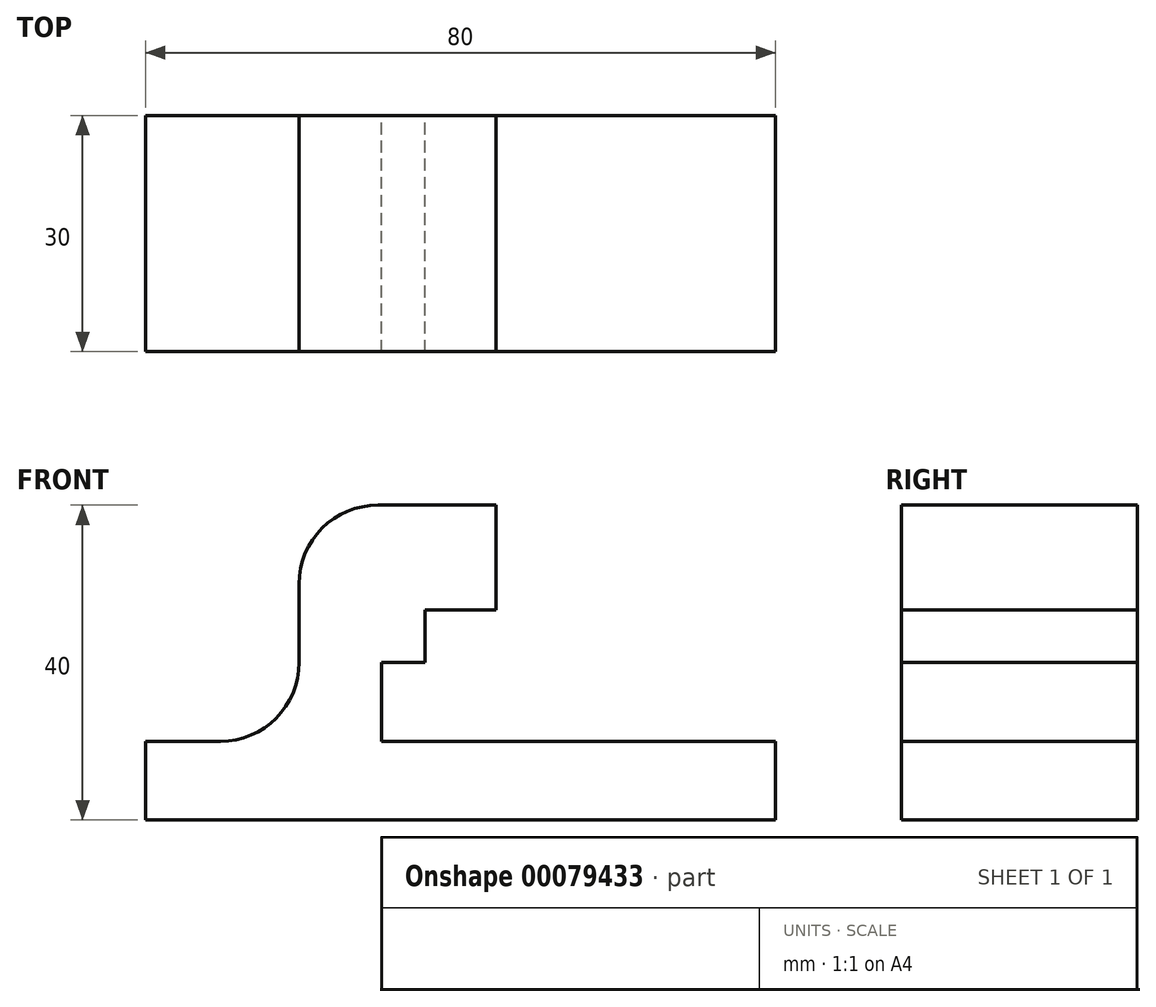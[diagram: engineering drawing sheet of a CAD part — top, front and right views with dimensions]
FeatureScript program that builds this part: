
annotation { "Feature Type Name" : "Feature", "Feature Type Description" : "" }
export const myFeature = defineFeature(function(context is Context, id is Id, definition is map)
    precondition{}
    {
        {
            var Q0;
            Q0=qCreatedBy(makeId("Front.planeOp"),FACE);
            var sketch = newSketch(context, id + "F0", { "sketchPlane" : qUnion([Q0])});
            skLineSegment(sketch, "E0", {"start": v(0, 0) * mm, "end": v(80, 0) * mm});
            skLineSegment(sketch, "E1", {"start": v(80, 0) * mm, "end": v(80, 10) * mm});
            skLineSegment(sketch, "E2", {"start": v(80, 10) * mm, "end": v(29.95, 10) * mm});
            skLineSegment(sketch, "E3", {"start": v(29.95, 10) * mm, "end": v(29.95, 20) * mm});
            skLineSegment(sketch, "E4", {"start": v(29.95, 20) * mm, "end": v(35.5, 20) * mm});
            skLineSegment(sketch, "E5", {"start": v(35.5, 20) * mm, "end": v(35.5, 26.7) * mm});
            skLineSegment(sketch, "E6", {"start": v(35.5, 26.7) * mm, "end": v(44.5, 26.7) * mm});
            skLineSegment(sketch, "E7", {"start": v(44.5, 26.7) * mm, "end": v(44.5, 40) * mm});
            skLineSegment(sketch, "E8", {"start": v(44.5, 40) * mm, "end": v(19.5, 40) * mm});
            skLineSegment(sketch, "E9", {"start": v(19.5, 40) * mm, "end": v(19.5, 10) * mm});
            skLineSegment(sketch, "E10", {"start": v(19.5, 10) * mm, "end": v(0, 10) * mm});
            skLineSegment(sketch, "E11", {"start": v(0, 10) * mm, "end": v(0, 0) * mm});
            skLineSegment(sketch, "E12", {"start": v(50.05, 10) * mm, "end": v(50.05, 0) * mm, "construction": true});
            skLineSegment(sketch, "E13", {"start": v(40, 0) * mm, "end": v(40, 26.7) * mm, "construction": true});
            skSolve(sketch);
        }
        {
            var Q0;
            Q0 = qSketchRegion(id + "F0", true);
            extrude(context, id + "F1", {"entities" : qUnion([Q0]), "depth" : 30 * mm});
        }
        {
            var Q0;
            Q0=makeQuery(id+"F1.opExtrude","SWEPT_EDGE",EDGE,{"disambiguationData":[OSD([sQuery(id+"F0.wireOp",EDGE,"E9"),sQuery(id+"F0.wireOp",EDGE,"E10")])]});
            var Q1;
            Q1=makeQuery(id+"F1.opExtrude","SWEPT_EDGE",EDGE,{"disambiguationData":[OSD([sQuery(id+"F0.wireOp",EDGE,"E8"),sQuery(id+"F0.wireOp",EDGE,"E9")])]});
            fillet(context, id + "F2", {"entities" : qUnion([Q0, Q1]), "radius" : 10 * mm, "tangentPropagation" : true, "allowEdgeOverflow" : false});
        }
    });
